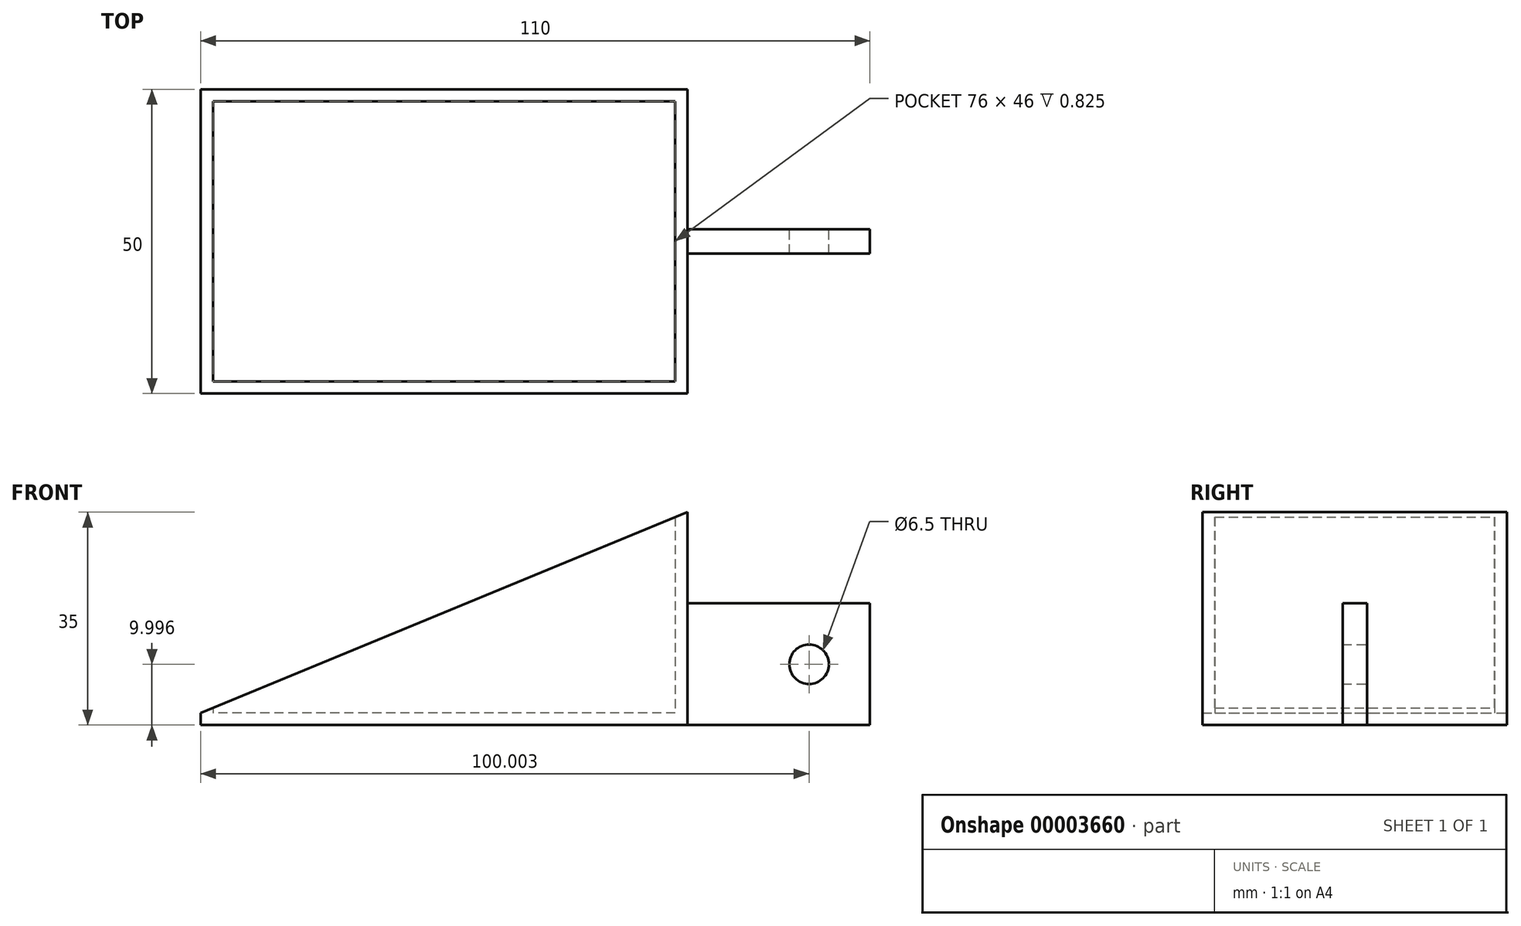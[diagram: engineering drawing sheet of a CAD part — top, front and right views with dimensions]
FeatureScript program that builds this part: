
annotation { "Feature Type Name" : "Feature", "Feature Type Description" : "" }
export const myFeature = defineFeature(function(context is Context, id is Id, definition is map)
    precondition{}
    {
        {
            var Q0;
            Q0=qCreatedBy(makeId("Front.planeOp"),FACE);
            var sketch = newSketch(context, id + "F0", { "sketchPlane" : qUnion([Q0])});
            skLineSegment(sketch, "E0", {"start": v(54.35, -24.4) * mm, "end": v(-55.65, -24.4) * mm});
            skLineSegment(sketch, "E1", {"start": v(-55.65, -22.4) * mm, "end": v(24.35, 10.6) * mm});
            skLineSegment(sketch, "E2", {"start": v(24.35, 10.6) * mm, "end": v(24.35, -4.4) * mm});
            skLineSegment(sketch, "E3", {"start": v(24.35, -4.4) * mm, "end": v(54.35, -4.4) * mm});
            skLineSegment(sketch, "E4", {"start": v(54.35, -4.4) * mm, "end": v(54.35, -24.4) * mm});
            skCircle(sketch, "E5", {"center": v(44.35, -14.4) * mm, "radius": 3.25 * mm});
            skLineSegment(sketch, "E6", {"start": v(-55.65, -22.4) * mm, "end": v(-55.65, -24.4) * mm});
            skLineSegment(sketch, "E7", {"start": v(24.35, -4.4) * mm, "end": v(24.35, -24.4) * mm});
            skSolve(sketch);
        }
        {
            var Q0;
            Q0=makeQuery(id+"F0.imprint","IMPRINT",FACE,{"disambiguationData":[TD([[makeQuery(id+"F0.imprint","IMPRINT",EDGE,{"derivedFrom":sQuery(id+"F0.wireOp",EDGE,"E1")}),-1.0]])]});
            extrude(context, id + "F1", {"entities" : qUnion([Q0]), "endBound" : BoundingType.SYMMETRIC, "depth" : 50 * mm});
        }
        {
            var Q0;
            Q0=makeQuery(id+"F0.imprint","IMPRINT",FACE,{"disambiguationData":[TD([[makeQuery(id+"F0.imprint","IMPRINT",EDGE,{"derivedFrom":sQuery(id+"F0.wireOp",EDGE,"E3")}),-1.0]])]});
            extrude(context, id + "F2", {"entities" : qUnion([Q0]), "operationType" : NewBodyOperationType.ADD, "endBound" : BoundingType.SYMMETRIC, "depth" : 4 * mm});
        }
        {
            var Q0;
            Q0=makeQuery(id+"F1.opExtrude","SWEPT_FACE",FACE,{"disambiguationData":[OSD([sQuery(id+"F0.wireOp",EDGE,"E1")])]});
            shell(context, id + "F3", {"entities" : qUnion([Q0]), "thickness" : 2 * mm});
        }
    });
